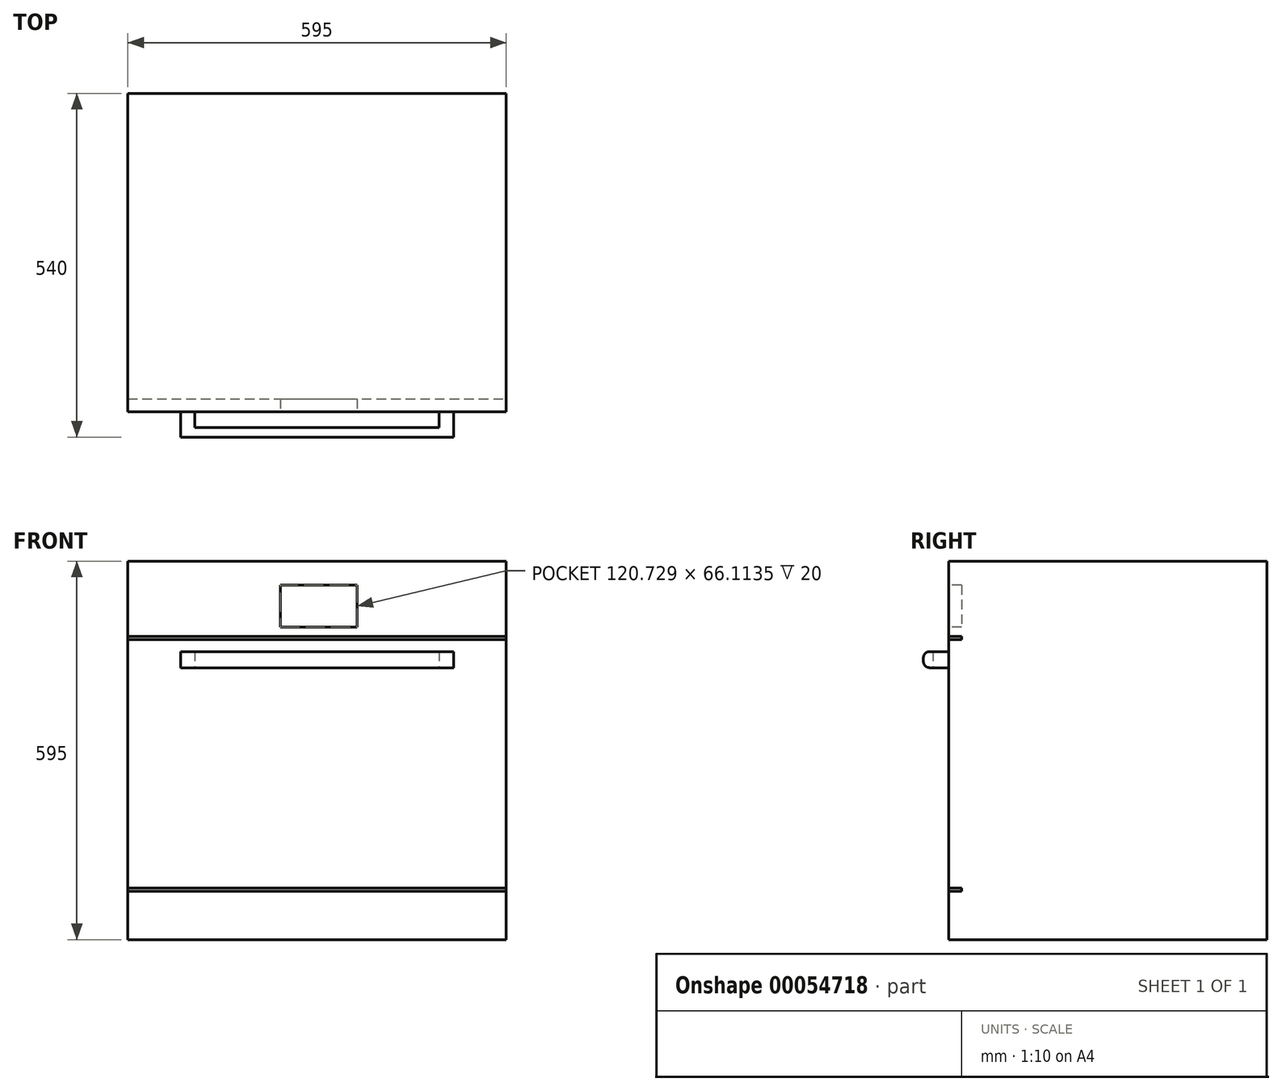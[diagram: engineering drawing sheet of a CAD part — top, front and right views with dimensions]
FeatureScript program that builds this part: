
annotation { "Feature Type Name" : "Feature", "Feature Type Description" : "" }
export const myFeature = defineFeature(function(context is Context, id is Id, definition is map)
    precondition{}
    {
        {
            var Q0;
            Q0=qCreatedBy(makeId("Front.planeOp"),FACE);
            var sketch = newSketch(context, id + "F0", { "sketchPlane" : qUnion([Q0])});
            skLineSegment(sketch, "E0.bottom", {"start": v(0, 0) * mm, "end": v(595, 0) * mm});
            skLineSegment(sketch, "E0.top", {"start": v(0, 595) * mm, "end": v(595, 595) * mm});
            skLineSegment(sketch, "E0.left", {"start": v(0, 0) * mm, "end": v(0, 595) * mm});
            skLineSegment(sketch, "E0.right", {"start": v(595, 0) * mm, "end": v(595, 595) * mm});
            skLineSegment(sketch, "E1.bottom", {"start": v(239.7, 557.25) * mm, "end": v(360.42, 557.25) * mm});
            skLineSegment(sketch, "E1.top", {"start": v(239.7, 491.13) * mm, "end": v(360.42, 491.13) * mm});
            skLineSegment(sketch, "E1.left", {"start": v(239.7, 557.25) * mm, "end": v(239.7, 491.13) * mm});
            skLineSegment(sketch, "E1.right", {"start": v(360.42, 557.25) * mm, "end": v(360.42, 491.13) * mm});
            skLineSegment(sketch, "E2.bottom", {"start": v(0, 476.82) * mm, "end": v(595, 476.82) * mm});
            skLineSegment(sketch, "E2.top", {"start": v(0, 471.82) * mm, "end": v(595, 471.82) * mm});
            skLineSegment(sketch, "E2.left", {"start": v(0, 476.82) * mm, "end": v(0, 471.82) * mm});
            skLineSegment(sketch, "E2.right", {"start": v(595, 476.82) * mm, "end": v(595, 471.82) * mm});
            skLineSegment(sketch, "E3.bottom", {"start": v(0, 81.2) * mm, "end": v(595, 81.2) * mm});
            skLineSegment(sketch, "E3.top", {"start": v(0, 76.2) * mm, "end": v(595, 76.2) * mm});
            skLineSegment(sketch, "E3.left", {"start": v(0, 81.2) * mm, "end": v(0, 76.2) * mm});
            skLineSegment(sketch, "E3.right", {"start": v(595, 81.2) * mm, "end": v(595, 76.2) * mm});
            skSolve(sketch);
        }
        {
            var Q0;
            Q0=makeQuery(id+"F0.imprint","IMPRINT",FACE,{"disambiguationData":[TD([[makeQuery(id+"F0.imprint","IMPRINT",EDGE,{"derivedFrom":sQuery(id+"F0.wireOp",EDGE,"E0.bottom")}),1.0]])]});
            var Q1;
            Q1=makeQuery(id+"F0.imprint","IMPRINT",FACE,{"disambiguationData":[TD([[makeQuery(id+"F0.imprint","IMPRINT",EDGE,{"derivedFrom":sQuery(id+"F0.wireOp",EDGE,"E3.bottom")}),-1.0]])]});
            var Q2;
            {var subQ0=sQuery(id+"F0.wireOp",EDGE,"E2.top");Q2=makeQuery(id+"F0.imprint","IMPRINT",FACE,{"disambiguationData":[TD([[makeQuery(id+"F0.imprint","IMPRINT",EDGE,{"derivedFrom":subQ0}),-1.0]])]});}
            var Q3;
            Q3=makeQuery(id+"F0.imprint","IMPRINT",FACE,{"disambiguationData":[TD([[makeQuery(id+"F0.imprint","IMPRINT",EDGE,{"derivedFrom":sQuery(id+"F0.wireOp",EDGE,"E2.bottom")}),-1.0]])]});
            var Q4;
            Q4=makeQuery(id+"F0.imprint","IMPRINT",FACE,{"disambiguationData":[TD([[makeQuery(id+"F0.imprint","IMPRINT",EDGE,{"derivedFrom":sQuery(id+"F0.wireOp",EDGE,"E1.bottom")}),-1.0]])]});
            var Q5;
            {var subQ0=sQuery(id+"F0.wireOp",EDGE,"E0.top");Q5=makeQuery(id+"F0.imprint","IMPRINT",FACE,{"disambiguationData":[TD([[makeQuery(id+"F0.imprint","IMPRINT",EDGE,{"derivedFrom":subQ0}),-1.0]])]});}
            extrude(context, id + "F1", {"entities" : qUnion([Q0, Q1, Q2, Q3, Q4, Q5]), "oppositeDirection" : true, "depth" : 500 * mm});
        }
        {
            var Q0;
            Q0=makeQuery(id+"F0.imprint","IMPRINT",FACE,{"disambiguationData":[TD([[makeQuery(id+"F0.imprint","IMPRINT",EDGE,{"derivedFrom":sQuery(id+"F0.wireOp",EDGE,"E1.bottom")}),-1.0]])]});
            var Q1;
            Q1=makeQuery(id+"F0.imprint","IMPRINT",FACE,{"disambiguationData":[TD([[makeQuery(id+"F0.imprint","IMPRINT",EDGE,{"derivedFrom":sQuery(id+"F0.wireOp",EDGE,"E2.bottom")}),-1.0]])]});
            var Q2;
            Q2=makeQuery(id+"F0.imprint","IMPRINT",FACE,{"disambiguationData":[TD([[makeQuery(id+"F0.imprint","IMPRINT",EDGE,{"derivedFrom":sQuery(id+"F0.wireOp",EDGE,"E3.bottom")}),-1.0]])]});
            extrude(context, id + "F2", {"entities" : qUnion([Q0, Q1, Q2]), "oppositeDirection" : true, "depth" : 20 * mm});
        }
        {
            var Q0;
            Q0=makeQuery(id+"F2.opExtrude","SWEPT_BODY",BODY,{"disambiguationData":[OSD([sQuery(id+"F0.wireOp",EDGE,"E1.bottom"),sQuery(id+"F0.wireOp",EDGE,"E1.top"),sQuery(id+"F0.wireOp",EDGE,"E1.left"),sQuery(id+"F0.wireOp",EDGE,"E1.right")])]});
            var Q1;
            Q1=makeQuery(id+"F2.opExtrude","SWEPT_BODY",BODY,{"disambiguationData":[OSD([sQuery(id+"F0.wireOp",EDGE,"E2.bottom"),sQuery(id+"F0.wireOp",EDGE,"E2.top"),sQuery(id+"F0.wireOp",EDGE,"E2.left"),sQuery(id+"F0.wireOp",EDGE,"E2.right")])]});
            var Q2;
            Q2=makeQuery(id+"F2.opExtrude","SWEPT_BODY",BODY,{"disambiguationData":[OSD([sQuery(id+"F0.wireOp",EDGE,"E3.bottom"),sQuery(id+"F0.wireOp",EDGE,"E3.top"),sQuery(id+"F0.wireOp",EDGE,"E3.left"),sQuery(id+"F0.wireOp",EDGE,"E3.right")])]});
            var Q3;
            Q3=makeQuery(id+"F1.opExtrude","SWEPT_BODY",BODY,{"disambiguationData":[OSD([sQuery(id+"F0.wireOp",EDGE,"E0.bottom"),sQuery(id+"F0.wireOp",EDGE,"E0.top"),sQuery(id+"F0.wireOp",EDGE,"E0.left"),sQuery(id+"F0.wireOp",EDGE,"E0.right"),sQuery(id+"F0.wireOp",EDGE,"E2.left"),sQuery(id+"F0.wireOp",EDGE,"E2.right"),sQuery(id+"F0.wireOp",EDGE,"E3.left"),sQuery(id+"F0.wireOp",EDGE,"E3.right")])]});
            booleanBodies(context, id + "F3", {"operationType" : BooleanOperationType.SUBTRACTION, "tools" : qUnion([Q0, Q1, Q2]), "targets" : qUnion([Q3]), "keepTools" : true});
        }
        {
            var Q0;
            Q0=makeQuery(id+"F1.opExtrude","SWEPT_FACE",FACE,{"disambiguationData":[OSD([sQuery(id+"F0.wireOp",EDGE,"E0.right"),sQuery(id+"F0.wireOp",EDGE,"E2.right"),sQuery(id+"F0.wireOp",EDGE,"E3.right")])]});
            var Q1;
            Q1=makeQuery(id+"F1.opExtrude","SWEPT_FACE",FACE,{"disambiguationData":[OSD([sQuery(id+"F0.wireOp",EDGE,"E0.left"),sQuery(id+"F0.wireOp",EDGE,"E2.left"),sQuery(id+"F0.wireOp",EDGE,"E3.left")])]});
            cPlane(context, id + "F4", {"entities" : qUnion([Q0, Q1]), "cplaneType" : CPlaneType.MID_PLANE, "offset" : 150 * mm, "width" : 150 * mm, "height" : 150 * mm});
        }
        {
            var Q0;
            {var subQ0=sQuery(id+"F0.wireOp",EDGE,"E2.top");Q0=makeQuery(id+"F0.imprint","IMPRINT",FACE,{"disambiguationData":[TD([[makeQuery(id+"F0.imprint","IMPRINT",EDGE,{"derivedFrom":subQ0}),-1.0]])]});}
            var sketch = newSketch(context, id + "F5", { "sketchPlane" : qUnion([Q0])});
            skLineSegment(sketch, "E4.bottom", {"start": v(82.87, 452.8) * mm, "end": v(105.26, 452.8) * mm});
            skLineSegment(sketch, "E4.top", {"start": v(82.87, 427.4) * mm, "end": v(105.26, 427.4) * mm});
            skLineSegment(sketch, "E4.left", {"start": v(82.87, 452.8) * mm, "end": v(82.87, 427.4) * mm});
            skLineSegment(sketch, "E4.right", {"start": v(105.26, 452.8) * mm, "end": v(105.26, 427.4) * mm});
            skLineSegment(sketch, "E5.MirrorCS", {"start": v(512.13, 452.8) * mm, "end": v(489.74, 452.8) * mm});
            skLineSegment(sketch, "E6.MirrorCS", {"start": v(489.74, 452.8) * mm, "end": v(489.74, 427.4) * mm});
            skLineSegment(sketch, "E7.MirrorCS", {"start": v(512.13, 427.4) * mm, "end": v(489.74, 427.4) * mm});
            skLineSegment(sketch, "E8.MirrorCS", {"start": v(512.13, 452.8) * mm, "end": v(512.13, 427.4) * mm});
            skSolve(sketch);
        }
        {
            var Q0;
            Q0=makeQuery(id+"F5.imprint","IMPRINT",FACE,{"disambiguationData":[TD([[makeQuery(id+"F5.imprint","IMPRINT",EDGE,{"derivedFrom":sQuery(id+"F5.wireOp",EDGE,"E4.bottom")}),-1.0]])]});
            var Q1;
            Q1=makeQuery(id+"F5.imprint","IMPRINT",FACE,{"disambiguationData":[TD([[makeQuery(id+"F5.imprint","IMPRINT",EDGE,{"derivedFrom":sQuery(id+"F5.wireOp",EDGE,"E5.MirrorCS")}),1.0]])]});
            extrude(context, id + "F6", {"entities" : qUnion([Q0, Q1]), "operationType" : NewBodyOperationType.ADD, "depth" : 25 * mm});
        }
        {
            var Q0;
            Q0=makeQuery(id+"F6.opExtrude","SWEPT_FACE",FACE,{"disambiguationData":[OSD([sQuery(id+"F5.wireOp",EDGE,"E4.left")])]});
            var sketch = newSketch(context, id + "F7", { "sketchPlane" : qUnion([Q0])});
            skLineSegment(sketch, "E9.bottom", {"start": v(25, 452.8) * mm, "end": v(40, 452.8) * mm});
            skLineSegment(sketch, "E9.top", {"start": v(25, 427.4) * mm, "end": v(40, 427.4) * mm});
            skLineSegment(sketch, "E9.left", {"start": v(25, 452.8) * mm, "end": v(25, 427.4) * mm});
            skLineSegment(sketch, "E9.right", {"start": v(40, 452.8) * mm, "end": v(40, 427.4) * mm});
            skSolve(sketch);
        }
        {
            var Q0;
            Q0=makeQuery(id+"F7.imprint","IMPRINT",FACE,{"disambiguationData":[TD([[makeQuery(id+"F7.imprint","IMPRINT",EDGE,{"derivedFrom":sQuery(id+"F7.wireOp",EDGE,"E9.bottom")}),-1.0]])]});
            var Q1;
            Q1=makeQuery(id+"F6.opExtrude","SWEPT_FACE",FACE,{"disambiguationData":[OSD([sQuery(id+"F5.wireOp",EDGE,"E8.MirrorCS")])]});
            extrude(context, id + "F8", {"entities" : qUnion([Q0]), "operationType" : NewBodyOperationType.ADD, "endBound" : BoundingType.UP_TO_SURFACE, "oppositeDirection" : true, "endBoundEntityFace" : qUnion([Q1]), "depth" : 25 * mm});
        }
        {
            var Q0;
            Q0=makeQuery(id+"F8.opExtrude","SWEPT_EDGE",EDGE,{"disambiguationData":[OSD([sQuery(id+"F7.wireOp",EDGE,"E9.bottom"),sQuery(id+"F7.wireOp",EDGE,"E9.right")])]});
            var Q1;
            Q1=makeQuery(id+"F8.opExtrude","SWEPT_EDGE",EDGE,{"disambiguationData":[OSD([sQuery(id+"F7.wireOp",EDGE,"E9.top"),sQuery(id+"F7.wireOp",EDGE,"E9.right")])]});
            fillet(context, id + "F9", {"entities" : qUnion([Q0, Q1]), "radius" : 10 * mm, "tangentPropagation" : true, "allowEdgeOverflow" : false});
        }
    });
